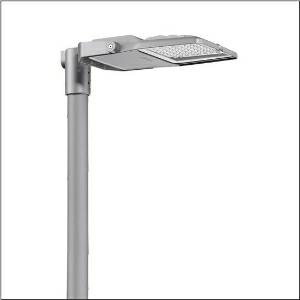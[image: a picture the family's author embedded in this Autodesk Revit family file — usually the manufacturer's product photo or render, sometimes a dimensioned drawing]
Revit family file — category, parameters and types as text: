
# Revit family: floodlight_fl_21_mini___pl43_5xa7771c4a3a_4cc4
name_source: partatom
category: Lighting Fixtures
units: mm (PartAtom-declared; Revit-internal decimal feet)

## family parameters
Cut with Voids When Loaded = No
Host = Face
Light Source = No
Part Type = Normal
Room Calculation Point = No
Round Connector Dimension = Use Diameter
Shared = No

## types (1)
- --- (1 x LED, 13050 lm, 87.2 W, 4000K)
    Apparent Load = 87 VA
    CIE Flux Codes = 27 78 99 100 100
    Color Rendering = 70
    Color Temperature = 4000K
    Default Elevation = 1800 mm
    Description = Floodlight FL 21 mini, floodlight, primary light control with lens, of PMMA, primary optical cover: protective disc, of toughened safety glass, transparent, light distribution: PL43, light emission: direct distribution, installation type: surface-mounted, LED, High Power LED, rated luminous flux: 13.050lm, luminous efficacy: 150lm/W, light colour: 740, colour temperature: 4000K, control gear: ECG iQ, control: Auto-Match, Temp-Guard, Lumen-Switch, Night-Set, Smart-Wire, Light-Fading, Desk-Remote (wireless, voltage-free reading and setting of iQ features in the workshop via application-optimized NFC function/RFID function), optimised constant luminous flux control (CLO 2.0), with terminal, 6-pole, mains connection: 220..240V, AC, 50/60Hz, start of lifetime: 87W, end of lifetime: 92W, reduction: 40W, luminaire housing, of diecast aluminium, powder-coated, Siteco® metallic grey (DB 702S), corrosivity category C5 according to DIN EN ISO 12944, mast bracket, of steel, galvanised, powder-coated, Siteco® metallic grey (DB 702S), protection rating (complete): IP66, insulation class (complete): insulation class II (safety insulation), certification: CE, ENEC, VDE, protection symbol: D, impact resistance: IK08, permissible operating ambient temperature: -40..+40°C, permissible operating ambient temperature for outdoor applications: -40..+50°C, standard: DIN EN 12944, packaging unit: 1 piece

Light Distribution: PL43
    Height = 70 mm
    Lamp = 1 x LED
    Lamp Light Flux = 13050 lm
    Lamp Power = 87.2 W
    Lamp count = 1
    Length = 485 mm
    Luminous efficacy = 150 lm/W
    Manufacturer = Siteco
    ModVariant = No
    Model = 5XA7771C4A3A
    Number of Poles = 1
    OnlyDefault = Yes
    Power Factor = 1
    Product Name = Floodlight FL 21 mini | PL43
    Product group = floodlight | pylon top
    ProductGroupID = 6101
    Protection Class = Protection class II
    Protection Degree = IP 66
    RLX_Detail_Level = 1
    RlxData = <blob elided: 100941 chars, md5=d9d95b50>
    Socket = socket
    Standby Power = 0 W
    System Light Flux = 13050 lm
    System Power = 87 W
    Type Comments = factory setting: luminous flux: 100 % | dim-lin: 254 | 456 mA
    Type Image = l_1007125.jpg
    URL = http://relux.com
    VarID = @adj_073617
    Voltage = 0 V
    Weight = 0.00 kg
    Width = 337 mm

## geometry (parser evidence)
native form markers: Blend x4, Sweep x11
no freeform markers — native parametric forms only
